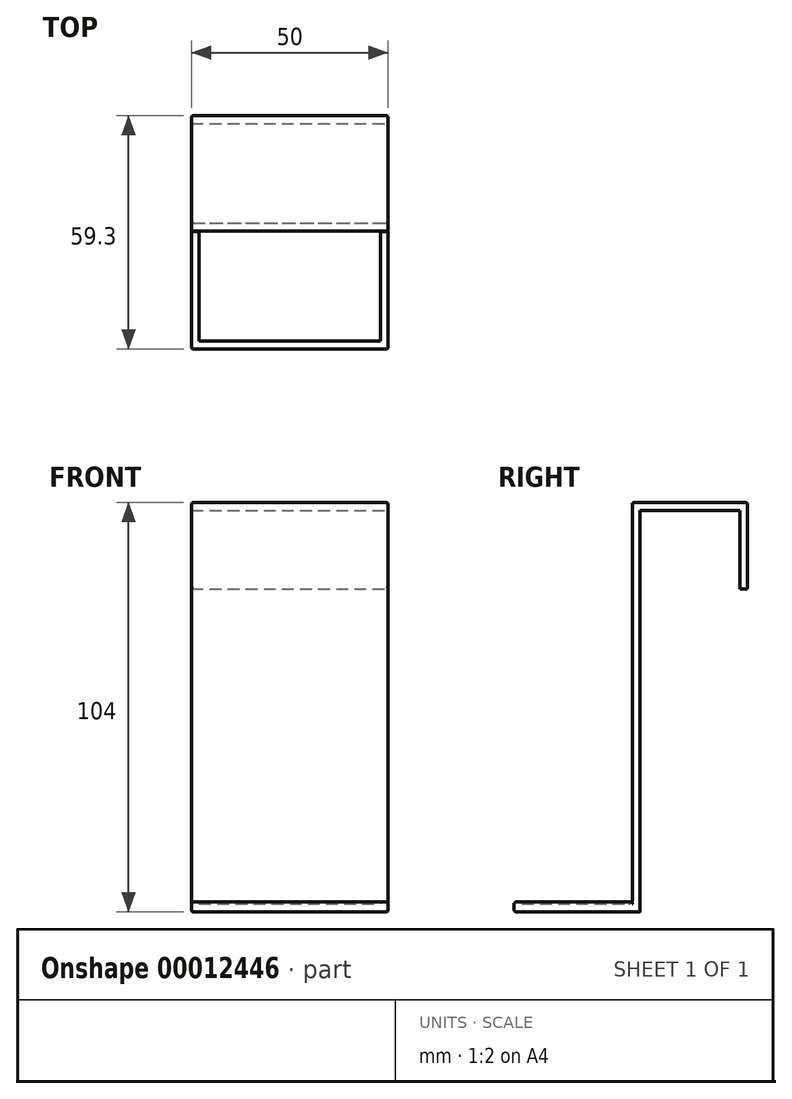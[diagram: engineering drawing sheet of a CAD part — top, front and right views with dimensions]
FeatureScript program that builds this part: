
annotation { "Feature Type Name" : "Feature", "Feature Type Description" : "" }
export const myFeature = defineFeature(function(context is Context, id is Id, definition is map)
    precondition{}
    {
        {
            var Q0;
            Q0=qCreatedBy(makeId("Right.planeOp"),FACE);
            var sketch = newSketch(context, id + "F0", { "sketchPlane" : qUnion([Q0])});
            skLineSegment(sketch, "E0", {"start": v(-30, 0) * mm, "end": v(0, 0) * mm});
            skLineSegment(sketch, "E1", {"start": v(0, 0) * mm, "end": v(0, 102) * mm});
            skLineSegment(sketch, "E2", {"start": v(0, 102) * mm, "end": v(29.3, 102) * mm});
            skLineSegment(sketch, "E3", {"start": v(29.3, 102) * mm, "end": v(29.3, 80) * mm});
            skLineSegment(sketch, "E4", {"start": v(-30, -2) * mm, "end": v(2, -2) * mm});
            skLineSegment(sketch, "E5", {"start": v(2, -2) * mm, "end": v(2, 100) * mm});
            skLineSegment(sketch, "E6", {"start": v(2, 100) * mm, "end": v(27.3, 100) * mm});
            skLineSegment(sketch, "E7", {"start": v(27.3, 100) * mm, "end": v(27.3, 80) * mm});
            skLineSegment(sketch, "E8", {"start": v(27.3, 80) * mm, "end": v(29.3, 80) * mm});
            skLineSegment(sketch, "E9", {"start": v(-30, 0) * mm, "end": v(-30, -2) * mm});
            skSolve(sketch);
        }
        {
            var Q0;
            Q0 = qSketchRegion(id + "F0", true);
            extrude(context, id + "F1", {"entities" : qUnion([Q0]), "oppositeDirection" : true, "depth" : 50 * mm});
        }
        {
            var Q0;
            Q0=makeQuery(id+"F1.opExtrude","SWEPT_FACE",FACE,{"disambiguationData":[OSD([sQuery(id+"F0.wireOp",EDGE,"E0")])]});
            var sketch = newSketch(context, id + "F2", { "sketchPlane" : qUnion([Q0])});
            skLineSegment(sketch, "E10.bottom", {"start": v(-50, 0) * mm, "end": v(-48, 0) * mm});
            skLineSegment(sketch, "E10.top", {"start": v(-50, -30) * mm, "end": v(-48, -30) * mm});
            skLineSegment(sketch, "E10.left", {"start": v(-50, 0) * mm, "end": v(-50, -30) * mm});
            skLineSegment(sketch, "E10.right", {"start": v(-48, 0) * mm, "end": v(-48, -30) * mm});
            skLineSegment(sketch, "E11.bottom", {"start": v(-50, -30) * mm, "end": v(0, -30) * mm});
            skLineSegment(sketch, "E11.top", {"start": v(-50, -28) * mm, "end": v(0, -28) * mm});
            skLineSegment(sketch, "E11.left", {"start": v(-50, -30) * mm, "end": v(-50, -28) * mm});
            skLineSegment(sketch, "E11.right", {"start": v(0, -30) * mm, "end": v(0, -28) * mm});
            skLineSegment(sketch, "E12.bottom", {"start": v(0, -30) * mm, "end": v(-2, -30) * mm});
            skLineSegment(sketch, "E12.top", {"start": v(0, 0) * mm, "end": v(-2, 0) * mm});
            skLineSegment(sketch, "E12.left", {"start": v(0, -30) * mm, "end": v(0, 0) * mm});
            skLineSegment(sketch, "E12.right", {"start": v(-2, -30) * mm, "end": v(-2, 0) * mm});
            skSolve(sketch);
        }
        {
            var Q0;
            Q0 = qSketchRegion(id + "F2", true);
            extrude(context, id + "F3", {"entities" : qUnion([Q0]), "operationType" : NewBodyOperationType.ADD, "depth" : 0.5 * mm});
        }
        {
            var Q0;
            Q0=makeQuery(id+"F3.opExtrude","CAP_EDGE",EDGE,{"disambiguationData":[OSD([sQuery(id+"F2.wireOp",EDGE,"E12.right")])],"isStart":true});
            var Q1;
            Q1=makeQuery(id+"F3.opExtrude","CAP_EDGE",EDGE,{"disambiguationData":[OSD([sQuery(id+"F2.wireOp",EDGE,"E11.top")])],"isStart":true});
            var Q2;
            Q2=makeQuery(id+"F3.opExtrude","CAP_EDGE",EDGE,{"disambiguationData":[OSD([sQuery(id+"F2.wireOp",EDGE,"E10.right")])],"isStart":true});
            var Q3;
            Q3=makeQuery(id+"F1.opExtrude","SWEPT_EDGE",EDGE,{"disambiguationData":[OSD([sQuery(id+"F0.wireOp",EDGE,"E0"),sQuery(id+"F0.wireOp",EDGE,"E1")])]});
            fillet(context, id + "F4", {"entities" : qUnion([Q0, Q1, Q2, Q3]), "radius" : 1 * mm, "tangentPropagation" : true, "allowEdgeOverflow" : false});
        }
        {
            var Q0;
            Q0=makeQuery(id+"F3.opExtrude","CAP_EDGE",EDGE,{"disambiguationData":[OSD([sQuery(id+"F2.wireOp",EDGE,"E12.left")])],"isStart":false});
            var Q1;
            {var subQ0=sQuery(id+"F2.wireOp",EDGE,"E12.right");Q1=makeQuery(id+"F4.opFillet","BLEND_EDGE",EDGE,{"blendedFrom":[makeQuery(id+"F3.opExtrude","CAP_EDGE",EDGE,{"disambiguationData":[OSD([subQ0])],"isStart":true}),makeQuery(id+"F3.opExtrude","CAP_FACE",FACE,{"disambiguationData":[OSD([sQuery(id+"F2.wireOp",EDGE,"E10.bottom"),sQuery(id+"F2.wireOp",EDGE,"E10.left"),sQuery(id+"F2.wireOp",EDGE,"E10.right"),sQuery(id+"F2.wireOp",EDGE,"E11.bottom"),sQuery(id+"F2.wireOp",EDGE,"E11.top"),sQuery(id+"F2.wireOp",EDGE,"E11.left"),sQuery(id+"F2.wireOp",EDGE,"E12.bottom"),sQuery(id+"F2.wireOp",EDGE,"E12.top"),sQuery(id+"F2.wireOp",EDGE,"E12.left"),subQ0])],"isStart":false})],"blendedInto":[makeQuery(id+"F3.opExtrude","CAP_FACE",FACE,{"disambiguationData":[OSD([sQuery(id+"F2.wireOp",EDGE,"E10.bottom"),sQuery(id+"F2.wireOp",EDGE,"E10.left"),sQuery(id+"F2.wireOp",EDGE,"E10.right"),sQuery(id+"F2.wireOp",EDGE,"E11.bottom"),sQuery(id+"F2.wireOp",EDGE,"E11.top"),sQuery(id+"F2.wireOp",EDGE,"E11.left"),sQuery(id+"F2.wireOp",EDGE,"E12.bottom"),sQuery(id+"F2.wireOp",EDGE,"E12.top"),sQuery(id+"F2.wireOp",EDGE,"E12.left"),subQ0])],"isStart":false})]});}
            var Q2;
            {var subQ0=sQuery(id+"F2.wireOp",EDGE,"E11.top");Q2=makeQuery(id+"F4.opFillet","BLEND_EDGE",EDGE,{"blendedFrom":[makeQuery(id+"F3.opExtrude","CAP_EDGE",EDGE,{"disambiguationData":[OSD([subQ0])],"isStart":true}),makeQuery(id+"F3.opExtrude","CAP_FACE",FACE,{"disambiguationData":[OSD([sQuery(id+"F2.wireOp",EDGE,"E10.bottom"),sQuery(id+"F2.wireOp",EDGE,"E10.left"),sQuery(id+"F2.wireOp",EDGE,"E10.right"),sQuery(id+"F2.wireOp",EDGE,"E11.bottom"),subQ0,sQuery(id+"F2.wireOp",EDGE,"E11.left"),sQuery(id+"F2.wireOp",EDGE,"E12.bottom"),sQuery(id+"F2.wireOp",EDGE,"E12.top"),sQuery(id+"F2.wireOp",EDGE,"E12.left"),sQuery(id+"F2.wireOp",EDGE,"E12.right")])],"isStart":false})],"blendedInto":[makeQuery(id+"F3.opExtrude","CAP_FACE",FACE,{"disambiguationData":[OSD([sQuery(id+"F2.wireOp",EDGE,"E10.bottom"),sQuery(id+"F2.wireOp",EDGE,"E10.left"),sQuery(id+"F2.wireOp",EDGE,"E10.right"),sQuery(id+"F2.wireOp",EDGE,"E11.bottom"),subQ0,sQuery(id+"F2.wireOp",EDGE,"E11.left"),sQuery(id+"F2.wireOp",EDGE,"E12.bottom"),sQuery(id+"F2.wireOp",EDGE,"E12.top"),sQuery(id+"F2.wireOp",EDGE,"E12.left"),sQuery(id+"F2.wireOp",EDGE,"E12.right")])],"isStart":false})]});}
            var Q3;
            Q3=makeQuery(id+"F3.opExtrude","CAP_EDGE",EDGE,{"disambiguationData":[OSD([sQuery(id+"F2.wireOp",EDGE,"E11.bottom"),sQuery(id+"F2.wireOp",EDGE,"E12.bottom")])],"isStart":false});
            var Q4;
            {var subQ0=sQuery(id+"F2.wireOp",EDGE,"E10.right");Q4=makeQuery(id+"F4.opFillet","BLEND_EDGE",EDGE,{"blendedFrom":[makeQuery(id+"F3.opExtrude","CAP_EDGE",EDGE,{"disambiguationData":[OSD([subQ0])],"isStart":true}),makeQuery(id+"F3.opExtrude","CAP_FACE",FACE,{"disambiguationData":[OSD([sQuery(id+"F2.wireOp",EDGE,"E10.bottom"),sQuery(id+"F2.wireOp",EDGE,"E10.left"),subQ0,sQuery(id+"F2.wireOp",EDGE,"E11.bottom"),sQuery(id+"F2.wireOp",EDGE,"E11.top"),sQuery(id+"F2.wireOp",EDGE,"E11.left"),sQuery(id+"F2.wireOp",EDGE,"E12.bottom"),sQuery(id+"F2.wireOp",EDGE,"E12.top"),sQuery(id+"F2.wireOp",EDGE,"E12.left"),sQuery(id+"F2.wireOp",EDGE,"E12.right")])],"isStart":false})],"blendedInto":[makeQuery(id+"F3.opExtrude","CAP_FACE",FACE,{"disambiguationData":[OSD([sQuery(id+"F2.wireOp",EDGE,"E10.bottom"),sQuery(id+"F2.wireOp",EDGE,"E10.left"),subQ0,sQuery(id+"F2.wireOp",EDGE,"E11.bottom"),sQuery(id+"F2.wireOp",EDGE,"E11.top"),sQuery(id+"F2.wireOp",EDGE,"E11.left"),sQuery(id+"F2.wireOp",EDGE,"E12.bottom"),sQuery(id+"F2.wireOp",EDGE,"E12.top"),sQuery(id+"F2.wireOp",EDGE,"E12.left"),sQuery(id+"F2.wireOp",EDGE,"E12.right")])],"isStart":false})]});}
            var Q5;
            Q5=makeQuery(id+"F3.opExtrude","CAP_EDGE",EDGE,{"disambiguationData":[OSD([sQuery(id+"F2.wireOp",EDGE,"E10.left"),sQuery(id+"F2.wireOp",EDGE,"E11.left")])],"isStart":false});
            var Q6;
            Q6=makeQuery(id+"F1.opExtrude","CAP_EDGE",EDGE,{"disambiguationData":[OSD([sQuery(id+"F0.wireOp",EDGE,"E1")])],"isStart":false});
            var Q7;
            Q7=makeQuery(id+"F1.opExtrude","CAP_EDGE",EDGE,{"disambiguationData":[OSD([sQuery(id+"F0.wireOp",EDGE,"E2")])],"isStart":false});
            var Q8;
            Q8=makeQuery(id+"F1.opExtrude","SWEPT_EDGE",EDGE,{"disambiguationData":[OSD([sQuery(id+"F0.wireOp",EDGE,"E1"),sQuery(id+"F0.wireOp",EDGE,"E2")])]});
            var Q9;
            Q9=makeQuery(id+"F1.opExtrude","CAP_EDGE",EDGE,{"disambiguationData":[OSD([sQuery(id+"F0.wireOp",EDGE,"E4")])],"isStart":false});
            var Q10;
            Q10=makeQuery(id+"F1.opExtrude","SWEPT_EDGE",EDGE,{"disambiguationData":[OSD([sQuery(id+"F0.wireOp",EDGE,"E4"),sQuery(id+"F0.wireOp",EDGE,"E9")])]});
            var Q11;
            Q11=makeQuery(id+"F1.opExtrude","CAP_EDGE",EDGE,{"disambiguationData":[OSD([sQuery(id+"F0.wireOp",EDGE,"E4")])],"isStart":true});
            var Q12;
            Q12=makeQuery(id+"F1.opExtrude","CAP_EDGE",EDGE,{"disambiguationData":[OSD([sQuery(id+"F0.wireOp",EDGE,"E1")])],"isStart":true});
            var Q13;
            Q13=makeQuery(id+"F1.opExtrude","CAP_EDGE",EDGE,{"disambiguationData":[OSD([sQuery(id+"F0.wireOp",EDGE,"E2")])],"isStart":true});
            var Q14;
            Q14=makeQuery(id+"F1.opExtrude","SWEPT_EDGE",EDGE,{"disambiguationData":[OSD([sQuery(id+"F0.wireOp",EDGE,"E2"),sQuery(id+"F0.wireOp",EDGE,"E3")])]});
            var Q15;
            Q15=makeQuery(id+"F1.opExtrude","CAP_EDGE",EDGE,{"disambiguationData":[OSD([sQuery(id+"F0.wireOp",EDGE,"E3")])],"isStart":true});
            var Q16;
            Q16=makeQuery(id+"F1.opExtrude","SWEPT_EDGE",EDGE,{"disambiguationData":[OSD([sQuery(id+"F0.wireOp",EDGE,"E3"),sQuery(id+"F0.wireOp",EDGE,"E8")])]});
            var Q17;
            Q17=makeQuery(id+"F1.opExtrude","CAP_EDGE",EDGE,{"disambiguationData":[OSD([sQuery(id+"F0.wireOp",EDGE,"E3")])],"isStart":false});
            var Q18;
            Q18=makeQuery(id+"F3.boolean.opBoolean","MERGE",EDGE,{"derivedFrom":[makeQuery(id+"F1.opExtrude","CAP_EDGE",EDGE,{"disambiguationData":[OSD([sQuery(id+"F0.wireOp",EDGE,"E9")])],"isStart":false}),makeQuery(id+"F3.opExtrude","SWEPT_EDGE",EDGE,{"disambiguationData":[OSD([sQuery(id+"F2.wireOp",EDGE,"E11.bottom"),sQuery(id+"F2.wireOp",EDGE,"E11.left")])]})]});
            var Q19;
            Q19=makeQuery(id+"F3.boolean.opBoolean","MERGE",EDGE,{"derivedFrom":[makeQuery(id+"F1.opExtrude","CAP_EDGE",EDGE,{"disambiguationData":[OSD([sQuery(id+"F0.wireOp",EDGE,"E9")])],"isStart":true}),makeQuery(id+"F3.opExtrude","SWEPT_EDGE",EDGE,{"disambiguationData":[OSD([sQuery(id+"F2.wireOp",EDGE,"E12.bottom"),sQuery(id+"F2.wireOp",EDGE,"E12.left")])]})]});
            fillet(context, id + "F5", {"entities" : qUnion([Q0, Q1, Q2, Q3, Q4, Q5, Q6, Q7, Q8, Q9, Q10, Q11, Q12, Q13, Q14, Q15, Q16, Q17, Q18, Q19]), "radius" : 0.5 * mm, "tangentPropagation" : true, "allowEdgeOverflow" : false});
        }
    });
